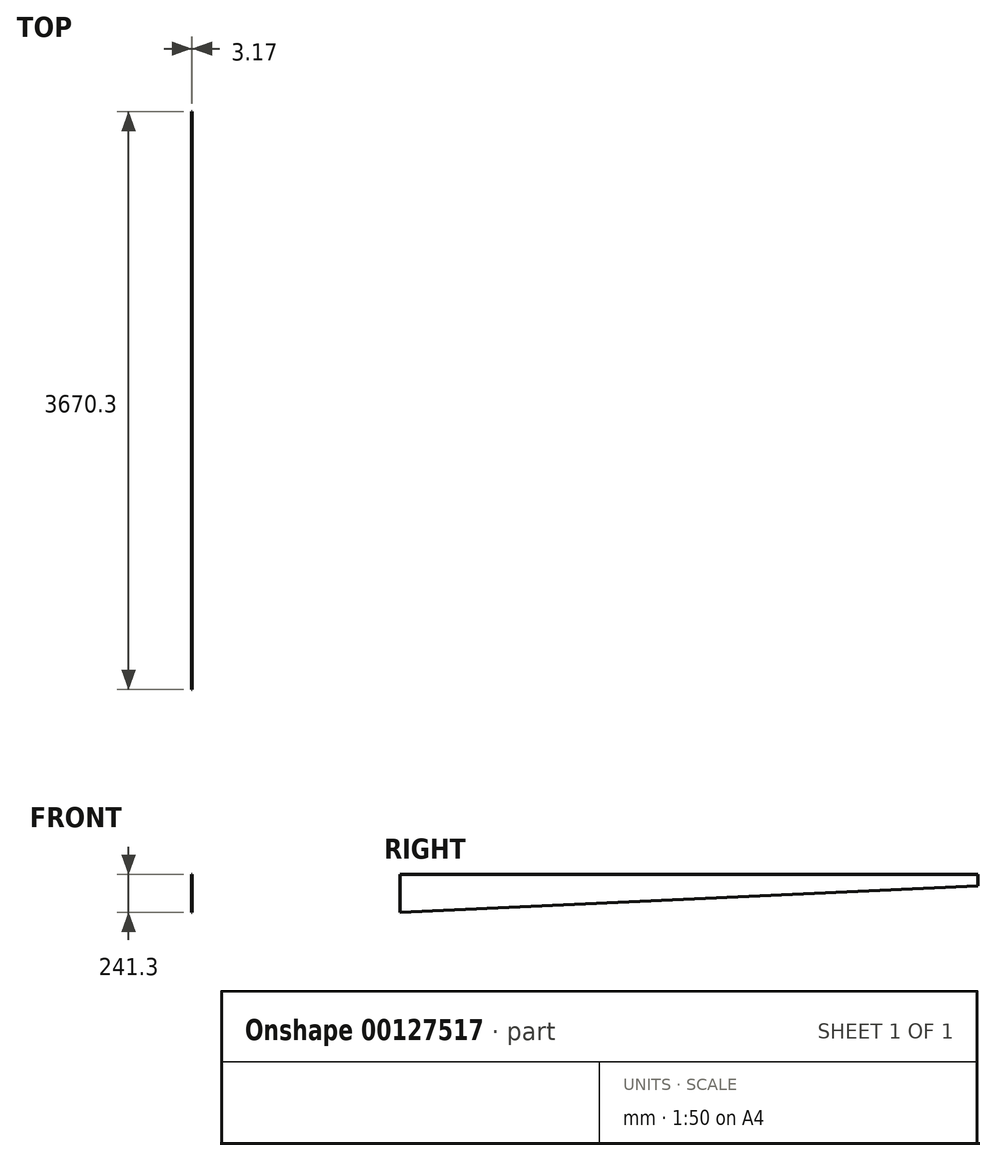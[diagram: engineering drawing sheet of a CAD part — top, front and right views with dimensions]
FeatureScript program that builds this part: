
annotation { "Feature Type Name" : "Feature", "Feature Type Description" : "" }
export const myFeature = defineFeature(function(context is Context, id is Id, definition is map)
    precondition{}
    {
        {
            var Q0;
            Q0=qCreatedBy(makeId("Right.planeOp"),FACE);
            var sketch = newSketch(context, id + "F0", { "sketchPlane" : qUnion([Q0])});
            skLineSegment(sketch, "E0", {"start": v(0, 0) * mm, "end": v(0, -241.3) * mm});
            skLineSegment(sketch, "E1", {"start": v(0, -241.3) * mm, "end": v(3670.3, -72.23) * mm});
            skLineSegment(sketch, "E2", {"start": v(3670.3, -72.23) * mm, "end": v(3670.3, 0) * mm});
            skLineSegment(sketch, "E3", {"start": v(3670.3, 0) * mm, "end": v(0, 0) * mm});
            skSolve(sketch);
        }
        {
            var Q0;
            Q0=qSketchRegion(id+"F0",true);
            extrude(context, id + "F1", {"entities" : qUnion([Q0]), "depth" : 3.17 * mm});
        }
        {
            var Q0;
            Q0=makeQuery(id+"F1.opExtrude","SWEPT_BODY",BODY,{"disambiguationData":[OSD([sQuery(id+"F0.wireOp",EDGE,"E0"),sQuery(id+"F0.wireOp",EDGE,"E1"),sQuery(id+"F0.wireOp",EDGE,"E2"),sQuery(id+"F0.wireOp",EDGE,"E3")])]});
            transform(context, id + "F2", {"entities" : qUnion([Q0]), "transformType" : TransformType.TRANSLATION_3D, "dx" : 0 * mm, "dy" : 0 * mm, "dz" : 0 * mm, "makeCopy" : true});
        }
    });
